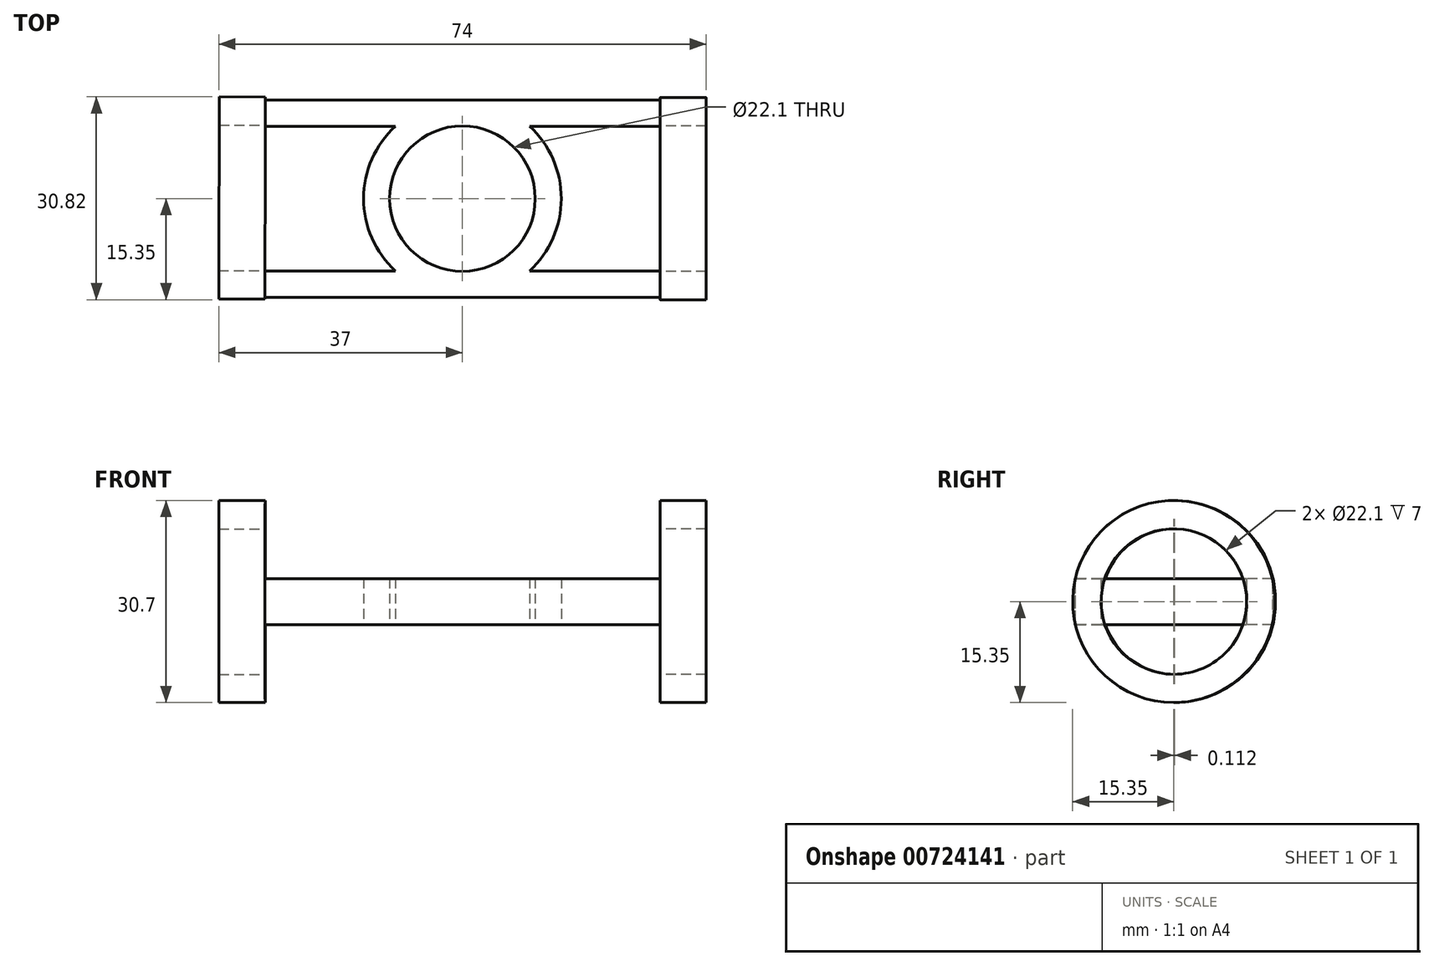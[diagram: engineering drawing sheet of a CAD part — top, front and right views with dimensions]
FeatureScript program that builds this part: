
annotation { "Feature Type Name" : "Feature", "Feature Type Description" : "" }
export const myFeature = defineFeature(function(context is Context, id is Id, definition is map)
    precondition{}
    {
        {
            var Q0;
            Q0=qCreatedBy(makeId("Top.planeOp"),FACE);
            var sketch = newSketch(context, id + "F0", { "sketchPlane" : qUnion([Q0])});
            skCircle(sketch, "E0", {"center": v(0, 0) * mm, "radius": 11.05 * mm});
            skCircle(sketch, "E1", {"center": v(0, 0) * mm, "radius": 15 * mm});
            skLineSegment(sketch, "E2", {"start": v(0, 15) * mm, "end": v(0, -15) * mm, "construction": true});
            skLineSegment(sketch, "E3", {"start": v(0, 15) * mm, "end": v(-30, 15) * mm});
            skLineSegment(sketch, "E4", {"start": v(0, -15) * mm, "end": v(-30, -15) * mm});
            skLineSegment(sketch, "E5", {"start": v(-10.2, 11) * mm, "end": v(-29.99, 11) * mm});
            skLineSegment(sketch, "E6", {"start": v(-10.2, -11) * mm, "end": v(-29.99, -11) * mm});
            skLineSegment(sketch, "E7", {"start": v(-30, -15) * mm, "end": v(-29.99, -11) * mm});
            skLineSegment(sketch, "E8", {"start": v(-29.99, 11) * mm, "end": v(-30, 15) * mm});
            skLineSegment(sketch, "E9", {"start": v(0, 15) * mm, "end": v(30, 15) * mm});
            skLineSegment(sketch, "E10", {"start": v(0, -15) * mm, "end": v(30, -15) * mm});
            skLineSegment(sketch, "E11", {"start": v(-30, 0) * mm, "end": v(-30, 15) * mm, "construction": true});
            skLineSegment(sketch, "E12", {"start": v(-30, 0) * mm, "end": v(-30, -15) * mm, "construction": true});
            skLineSegment(sketch, "E13", {"start": v(0, 0) * mm, "end": v(30, 0) * mm, "construction": true});
            skLineSegment(sketch, "E14", {"start": v(30, 0) * mm, "end": v(30, -15) * mm, "construction": true});
            skLineSegment(sketch, "E15", {"start": v(30, 0) * mm, "end": v(30, 15) * mm, "construction": true});
            skLineSegment(sketch, "E16", {"start": v(10.2, 11) * mm, "end": v(30, 11) * mm});
            skLineSegment(sketch, "E17", {"start": v(30, 15) * mm, "end": v(30, 11) * mm});
            skLineSegment(sketch, "E18", {"start": v(10.2, -11) * mm, "end": v(30, -11) * mm});
            skLineSegment(sketch, "E19", {"start": v(30, -11) * mm, "end": v(30, -15) * mm});
            skSolve(sketch);
        }
        {
            var Q0;
            Q0 = qSketchRegion(id + "F0", true);
            extrude(context, id + "F1", {"entities" : qUnion([Q0]), "depth" : 7 * mm, "offsetDistance" : 25 * mm});
        }
        {
            var Q0;
            Q0=makeQuery(id+"F1.opExtrude","SWEPT_FACE",FACE,{"disambiguationData":[OSD([sQuery(id+"F0.wireOp",EDGE,"E7")])]});
            var sketch = newSketch(context, id + "F2", { "sketchPlane" : qUnion([Q0])});
            skLineSegment(sketch, "E20", {"start": v(0, 0) * mm, "end": v(0, 3.5) * mm, "construction": true});
            skCircle(sketch, "E21", {"center": v(0, 3.5) * mm, "radius": 11.05 * mm});
            skCircle(sketch, "E22", {"center": v(0, 3.5) * mm, "radius": 15.35 * mm});
            skSolve(sketch);
        }
        {
            var Q0;
            Q0 = qSketchRegion(id + "F2", true);
            extrude(context, id + "F3", {"entities" : qUnion([Q0]), "operationType" : NewBodyOperationType.ADD, "depth" : 7 * mm, "offsetDistance" : 25 * mm});
        }
        {
            var Q0;
            Q0=makeQuery(id+"F1.opExtrude","SWEPT_FACE",FACE,{"disambiguationData":[OSD([sQuery(id+"F0.wireOp",EDGE,"E17")])]});
            var sketch = newSketch(context, id + "F4", { "sketchPlane" : qUnion([Q0])});
            skLineSegment(sketch, "E23", {"start": v(0, 0) * mm, "end": v(0, 3.5) * mm, "construction": true});
            skCircle(sketch, "E24", {"center": v(0, 3.5) * mm, "radius": 11.05 * mm});
            skCircle(sketch, "E25", {"center": v(0, 3.5) * mm, "radius": 15.35 * mm});
            skSolve(sketch);
        }
        {
            var Q0;
            Q0 = qSketchRegion(id + "F4", true);
            extrude(context, id + "F5", {"entities" : qUnion([Q0]), "operationType" : NewBodyOperationType.ADD, "depth" : 7 * mm, "offsetDistance" : 25 * mm});
        }
    });
